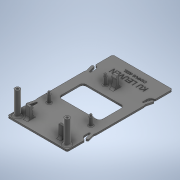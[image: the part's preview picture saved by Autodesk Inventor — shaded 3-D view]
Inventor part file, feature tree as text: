
AUTODESK INVENTOR PART (.ipt)
format: ipt  version: 2022 (Build 260153000, 153)  size: 772,096 bytes
history: native  units: mm
features: sketch x10, extrude x9, fillet x4, plane x3, mirror x3, emboss x1
ambient origin geometry x8: Origin, YZ Plane, XZ Plane, XY Plane, X Axis, Y Axis, Z Axis, Center Point
bodies: Solid1 (feature_tree)
feature tree (30):
  extrude  "Extrusion1"  Depth=127.0mm
  extrude  "Extrusion8"  Depth=4.0mm
  fillet  "Fillet3"  Radius=9.0mm
  extrude  "Extrusion9"  Depth=2.5mm
  fillet  "Fillet4"  Radius=2.5mm
  fillet  "Fillet5"  Radius=2.5mm
  plane  "Work Plane1"
  extrude  "Extrusion11"  Depth=3.0mm
  plane  "Work Plane2"
  mirror  "Mirror1"
  extrude  "Extrusion12"  Depth=2.0mm
  extrude  "Extrusion13"  Depth=29.0mm
  fillet  "Fillet6"  Radius=10.5mm
  extrude  "Extrusion14"  Depth=10.5mm
  emboss  "Emboss2"
  extrude  "Extrusion15"  Depth=11.0mm
  extrude  "Extrusion16"  Depth=10.0mm
  plane  "Work Plane3"
  mirror  "Mirror4"
  mirror  "Mirror5"
  sketch  "Sketch1"  dims[d0=72.0mm d1=127.0mm]
  sketch  "Sketch2"  dims[d2=2.0mm d3=0.0mm d34=4.0mm d62=9.0mm d63=0.0mm]
  sketch  "Sketch8"  dims[d64=1.0mm d65=2.5mm d66=2.5mm d67=2.5mm]
  sketch  "Sketch10"  dims[d68=3.0mm d69=0.0mm d70=0.5mm]
  sketch  "Sketch11"  dims[d82=2.0mm d83=70.0mm]
  sketch  "Sketch12"  dims[d84=82.45mm d85=29.0mm d86=10.5mm]
  sketch  "Sketch13"  dims[d87=25.8mm d88=10.5mm]
  sketch  "Sketch16"  dims[d89=2.3mm d90=11.0mm]
  sketch  "Sketch19"  dims[d91=-16.0mm d92=10.0mm]
  sketch  "Sketch20"  dims[d96=1.0mm d98=3.0mm d100=2.5mm d102=1.5mm d103=3.0mm d105=5.0mm d106=0.0mm d107=10.0mm d109=2.5mm d112=3.0mm d113=3.0mm d115=5.0mm d116=0.0mm d117=10.9mm d118=1.0mm d119=1.5mm d120=10.9mm d121=5.5mm d122=82.45mm d123=27.7mm d124=50.0mm d125=30.0mm d126=50.0mm d127=4.0mm d128=6.0mm d129=6.0mm d130=6.0mm d131=6.0mm d132=6.0mm d133=28.0mm d134=0.0mm d135=2.0mm d136=2.5mm d137=2.5mm d138=10.0mm d139=0.0mm d162=5.0mm d163=1.0mm d164=0.0mm d182=5.0mm d185=20.0mm d188=15.0mm d193=0.0mm d194=0.0mm d195=3.0mm d196=4.0mm d197=3.0mm d199=1.5mm d200=15.0deg d201=6.0mm d202=1.5mm d203=0.0mm d204=0.0mm]
